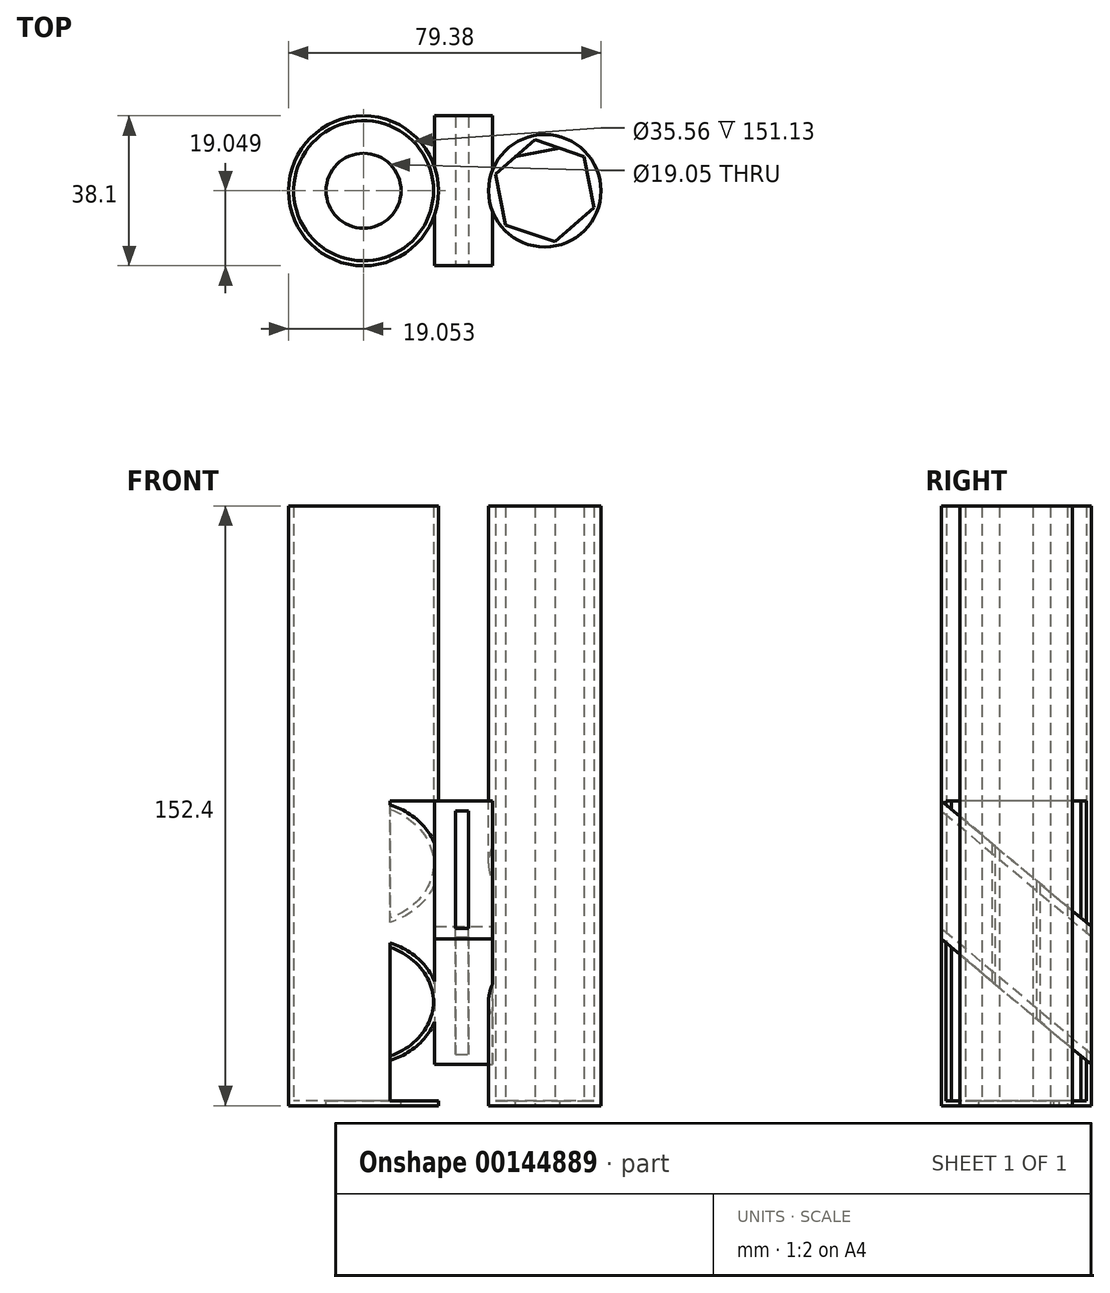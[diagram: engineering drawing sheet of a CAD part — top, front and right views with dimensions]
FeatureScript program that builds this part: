
annotation { "Feature Type Name" : "Feature", "Feature Type Description" : "" }
export const myFeature = defineFeature(function(context is Context, id is Id, definition is map)
    precondition{}
    {
        {
            var Q0;
            Q0=qCreatedBy(makeId("Top.planeOp"),FACE);
            var sketch = newSketch(context, id + "F0", { "sketchPlane" : qUnion([Q0])});
            skCircle(sketch, "E0", {"center": v(-55.59, 34.79) * mm, "radius": 9.53 * mm});
            skCircle(sketch, "E1", {"center": v(-55.59, 34.79) * mm, "radius": 17.78 * mm});
            skCircle(sketch, "E2.0", {"center": v(-55.59, 34.79) * mm, "radius": 19.05 * mm});
            skCircle(sketch, "E3.cCircle", {"center": v(-9.55, 34.79) * mm, "radius": 11.43 * mm, "construction": true});
            skLineSegment(sketch, "E3.0", {"start": v(-7.01, 21.84) * mm, "end": v(-19.5, 26.11) * mm});
            skLineSegment(sketch, "E3.1", {"start": v(-19.5, 26.11) * mm, "end": v(-22.03, 39.07) * mm});
            skLineSegment(sketch, "E3.2", {"start": v(-22.03, 39.07) * mm, "end": v(-12.09, 47.74) * mm});
            skLineSegment(sketch, "E3.3", {"start": v(-12.09, 47.74) * mm, "end": v(0.4, 43.46) * mm});
            skLineSegment(sketch, "E3.4", {"start": v(0.4, 43.46) * mm, "end": v(2.94, 30.51) * mm});
            skLineSegment(sketch, "E3.5", {"start": v(2.94, 30.51) * mm, "end": v(-7.01, 21.84) * mm});
            skPoint(sketch, "E3.0.midPoint", {"position": v(-13.25, 23.98) * mm});
            skCircle(sketch, "E4", {"center": v(-9.55, 34.79) * mm, "radius": 14.29 * mm});
            skLineSegment(sketch, "E5", {"start": v(-55.59, 34.79) * mm, "end": v(36.92, 34.79) * mm, "construction": true});
            skLineSegment(sketch, "E6", {"start": v(-23.84, 34.79) * mm, "end": v(-23.84, 53.84) * mm});
            skLineSegment(sketch, "E7", {"start": v(-36.54, 34.79) * mm, "end": v(-36.54, 15.74) * mm});
            skLineSegment(sketch, "E8", {"start": v(-36.54, 15.74) * mm, "end": v(-23.84, 15.74) * mm});
            skLineSegment(sketch, "E9", {"start": v(-23.84, 15.74) * mm, "end": v(-23.84, 34.79) * mm});
            skLineSegment(sketch, "E10", {"start": v(-36.54, 34.79) * mm, "end": v(-36.54, 53.84) * mm});
            skLineSegment(sketch, "E11", {"start": v(-36.54, 53.84) * mm, "end": v(-23.84, 53.84) * mm});
            skSolve(sketch);
        }
        {
            var Q0;
            Q0=makeQuery(id+"F0.imprint","IMPRINT",FACE,{"disambiguationData":[TD([[makeQuery(id+"F0.imprint","IMPRINT",EDGE,{"derivedFrom":sQuery(id+"F0.wireOp",EDGE,"E3.0")}),1.0]])]});
            var Q1;
            Q1=makeQuery(id+"F0.imprint","IMPRINT",FACE,{"disambiguationData":[TD([[makeQuery(id+"F0.imprint","IMPRINT",EDGE,{"derivedFrom":sQuery(id+"F0.wireOp",EDGE,"E3.0")}),-1.0]])]});
            var Q2;
            Q2=makeQuery(id+"F0.imprint","IMPRINT",FACE,{"disambiguationData":[TD([[makeQuery(id+"F0.imprint","IMPRINT",EDGE,{"derivedFrom":sQuery(id+"F0.wireOp",EDGE,"E0")}),-1.0]])]});
            var Q3;
            Q3=makeQuery(id+"F0.imprint","IMPRINT",FACE,{"disambiguationData":[TD([[makeQuery(id+"F0.imprint","IMPRINT",EDGE,{"derivedFrom":sQuery(id+"F0.wireOp",EDGE,"E1")}),-1.0]])]});
            extrude(context, id + "F1", {"entities" : qUnion([Q0, Q1, Q2, Q3]), "oppositeDirection" : true, "depth" : 1.27 * mm});
        }
        {
            var Q0;
            Q0=makeQuery(id+"F0.imprint","IMPRINT",FACE,{"disambiguationData":[TD([[makeQuery(id+"F0.imprint","IMPRINT",EDGE,{"derivedFrom":sQuery(id+"F0.wireOp",EDGE,"E1")}),-1.0]])]});
            var Q1;
            Q1=makeQuery(id+"F0.imprint","IMPRINT",FACE,{"disambiguationData":[TD([[makeQuery(id+"F0.imprint","IMPRINT",EDGE,{"derivedFrom":sQuery(id+"F0.wireOp",EDGE,"E3.0")}),1.0]])]});
            extrude(context, id + "F2", {"entities" : qUnion([Q0, Q1]), "operationType" : NewBodyOperationType.ADD, "depth" : 151.13 * mm});
        }
        {
            var Q0;
            Q0=makeQuery(id+"F0.imprint","IMPRINT",FACE,{"disambiguationData":[TD([[makeQuery(id+"F0.imprint","IMPRINT",EDGE,{"derivedFrom":sQuery(id+"F0.wireOp",EDGE,"E6")}),1.0]])]});
            extrude(context, id + "F3", {"entities" : qUnion([Q0]), "depth" : 76.2 * mm});
        }
        {
            var Q0;
            Q0=makeQuery(id+"F3.opExtrude","SWEPT_FACE",FACE,{"disambiguationData":[OSD([sQuery(id+"F0.wireOp",EDGE,"E6"),sQuery(id+"F0.wireOp",EDGE,"E9")])]});
            var sketch = newSketch(context, id + "F4", { "sketchPlane" : qUnion([Q0])});
            skLineSegment(sketch, "E12", {"start": v(53.84, 41.62) * mm, "end": v(15.74, 73.59) * mm});
            skLineSegment(sketch, "E13.0", {"start": v(53.84, 11.78) * mm, "end": v(15.74, 43.75) * mm});
            skLineSegment(sketch, "E14.0", {"start": v(53.84, 44.23) * mm, "end": v(15.74, 76.2) * mm});
            skLineSegment(sketch, "E15.0", {"start": v(53.84, 9.17) * mm, "end": v(15.74, 41.14) * mm});
            skSolve(sketch);
        }
        {
            var Q0;
            {var subQ1=sQuery(id+"F0.wireOp",EDGE,"E9");var subQ2=sQuery(id+"F0.wireOp",EDGE,"E6");var subQ3=makeQuery(id+"F3.opExtrude","CAP_EDGE",EDGE,{"disambiguationData":[OSD([subQ2,subQ1])],"isStart":false});Q0=makeQuery(id+"F4.imprint","IMPRINT",FACE,{"disambiguationData":[TD([[makeQuery(id+"F4.imprint","IMPRINT",EDGE,{"derivedFrom":subQ3}),-1.0]])]});}
            var Q1;
            {var subQ0=sQuery(id+"F4.wireOp",EDGE,"E15.0");Q1=makeQuery(id+"F4.imprint","IMPRINT",FACE,{"disambiguationData":[TD([[makeQuery(id+"F4.imprint","IMPRINT",EDGE,{"derivedFrom":subQ0}),1.0]])]});}
            extrude(context, id + "F5", {"entities" : qUnion([Q0, Q1]), "operationType" : NewBodyOperationType.REMOVE, "oppositeDirection" : true, "depth" : 25 * mm});
        }
        {
            var Q0;
            {var subQ0=sQuery(id+"F4.wireOp",EDGE,"E12");Q0=makeQuery(id+"F4.imprint","IMPRINT",FACE,{"disambiguationData":[TD([[makeQuery(id+"F4.imprint","IMPRINT",EDGE,{"derivedFrom":subQ0}),1.0]])]});}
            extrude(context, id + "F6", {"entities" : qUnion([Q0]), "operationType" : NewBodyOperationType.REMOVE, "oppositeDirection" : true, "depth" : 8.38 * mm, "hasSecondDirection" : true, "secondDirectionOppositeDirection" : true, "secondDirectionDepth" : 5.08 * mm});
        }
        {
            var Q0;
            Q0=makeQuery(id+"F3.opExtrude","SWEPT_FACE",FACE,{"disambiguationData":[OSD([sQuery(id+"F0.wireOp",EDGE,"E7"),sQuery(id+"F0.wireOp",EDGE,"E10")])]});
            extrude(context, id + "F7", {"entities" : qUnion([Q0]), "operationType" : NewBodyOperationType.ADD, "depth" : 1 * mm});
        }
        {
            var Q0;
            Q0=makeQuery(id+"F3.opExtrude","SWEPT_FACE",FACE,{"disambiguationData":[OSD([sQuery(id+"F0.wireOp",EDGE,"E6"),sQuery(id+"F0.wireOp",EDGE,"E9")])]});
            extrude(context, id + "F8", {"entities" : qUnion([Q0]), "operationType" : NewBodyOperationType.ADD, "depth" : 1 * mm});
        }
        {
            var Q0;
            Q0=makeQuery(id+"F1.opExtrude","CAP_FACE",FACE,{"disambiguationData":[OSD([sQuery(id+"F0.wireOp",EDGE,"E4")])],"isStart":false});
            var sketch = newSketch(context, id + "F9", { "sketchPlane" : qUnion([Q0])});
            skLineSegment(sketch, "E16.0.0", {"start": v(2.94, -30.51) * mm, "end": v(0.4, -43.46) * mm});
            skLineSegment(sketch, "E16.0.1", {"start": v(0.4, -43.46) * mm, "end": v(-12.09, -47.74) * mm});
            skLineSegment(sketch, "E16.0.2", {"start": v(-12.09, -47.74) * mm, "end": v(-22.03, -39.07) * mm});
            skLineSegment(sketch, "E16.0.3", {"start": v(-22.03, -39.07) * mm, "end": v(-19.5, -26.11) * mm});
            skLineSegment(sketch, "E16.0.4", {"start": v(-19.5, -26.11) * mm, "end": v(-7.01, -21.84) * mm});
            skLineSegment(sketch, "E16.0.5", {"start": v(-7.01, -21.84) * mm, "end": v(2.94, -30.51) * mm});
            skLineSegment(sketch, "E17", {"start": v(-5.84, -45.6) * mm, "end": v(-17.06, -43.4) * mm});
            skSolve(sketch);
        }
        {
            var Q0;
            {var subQ3=sQuery(id+"F9.wireOp",EDGE,"E17");Q0=makeQuery(id+"F9.imprint","IMPRINT",FACE,{"disambiguationData":[TD([[makeQuery(id+"F9.imprint","IMPRINT",EDGE,{"derivedFrom":subQ3}),1.0]])]});}
            extrude(context, id + "F10", {"entities" : qUnion([Q0]), "operationType" : NewBodyOperationType.REMOVE, "oppositeDirection" : true, "depth" : 25 * mm});
        }
    });
